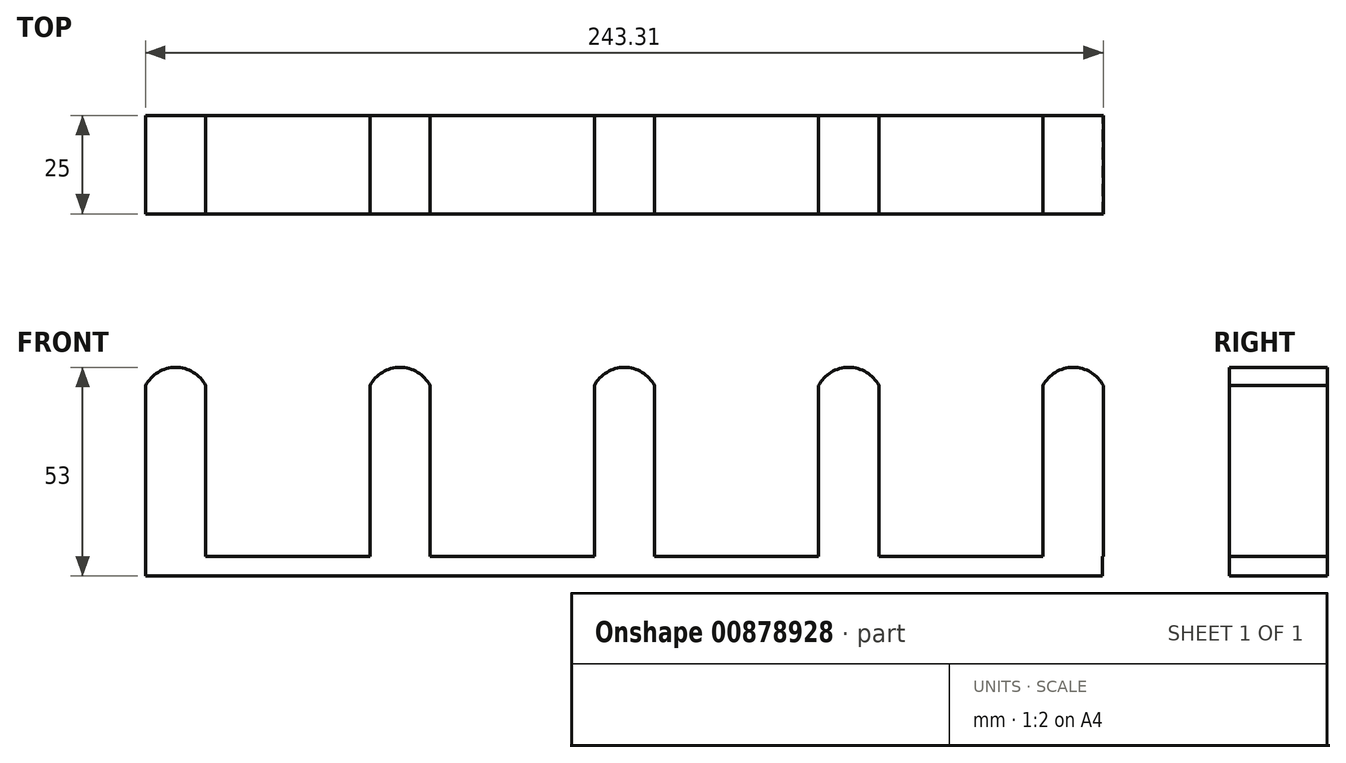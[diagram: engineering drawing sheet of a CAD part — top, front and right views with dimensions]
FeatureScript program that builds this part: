
annotation { "Feature Type Name" : "Feature", "Feature Type Description" : "" }
export const myFeature = defineFeature(function(context is Context, id is Id, definition is map)
    precondition{}
    {
        {
            var Q0;
            Q0=qCreatedBy(makeId("Front.planeOp"),FACE);
            var sketch = newSketch(context, id + "F0", { "sketchPlane" : qUnion([Q0])});
            skLineSegment(sketch, "E0", {"start": v(-65.05, 0) * mm, "end": v(83.37, 0) * mm});
            skLineSegment(sketch, "E1", {"start": v(-49.51, 48) * mm, "end": v(-49.51, -43.14) * mm, "construction": true});
            skLineSegment(sketch, "E2", {"start": v(-57.17, 0) * mm, "end": v(-57.17, 43.37) * mm});
            skLineSegment(sketch, "E3.MirrorCS", {"start": v(-41.86, 0) * mm, "end": v(-41.86, 43.37) * mm});
            skArc(sketch, "E4", {"start": v(-41.86, 43.37) * mm, "mid": v(-49.51, 48) * mm, "end": v(-57.17, 43.37) * mm});
            skLineSegment(sketch, "E5.1.0.0", {"start": v(-8.05, 0) * mm, "end": v(140.37, 0) * mm});
            skLineSegment(sketch, "E5.1.0.1", {"start": v(15.14, 0) * mm, "end": v(15.14, 43.37) * mm});
            skArc(sketch, "E5.1.0.2", {"start": v(15.14, 43.37) * mm, "mid": v(7.49, 48) * mm, "end": v(-0.17, 43.37) * mm});
            skLineSegment(sketch, "E5.1.0.3", {"start": v(-0.17, 0) * mm, "end": v(-0.17, 43.37) * mm});
            skLineSegment(sketch, "E5.1.0.4", {"start": v(7.49, 48) * mm, "end": v(7.49, -43.14) * mm, "construction": true});
            skLineSegment(sketch, "E5.2.0.0", {"start": v(48.95, 0) * mm, "end": v(197.37, 0) * mm});
            skLineSegment(sketch, "E5.2.0.1", {"start": v(72.14, 0) * mm, "end": v(72.14, 43.37) * mm});
            skArc(sketch, "E5.2.0.2", {"start": v(72.14, 43.37) * mm, "mid": v(64.49, 48) * mm, "end": v(56.83, 43.37) * mm});
            skLineSegment(sketch, "E5.2.0.3", {"start": v(56.83, 0) * mm, "end": v(56.83, 43.37) * mm});
            skLineSegment(sketch, "E5.2.0.4", {"start": v(64.49, 48) * mm, "end": v(64.49, -43.14) * mm, "construction": true});
            skLineSegment(sketch, "E5.direction1", {"start": v(-65.05, 0) * mm, "end": v(-8.05, 0) * mm, "construction": true});
            skLineSegment(sketch, "E6.bottom", {"start": v(-57.17, 0) * mm, "end": v(72.14, 0) * mm});
            skLineSegment(sketch, "E7.0.3.0", {"start": v(105.95, 0) * mm, "end": v(254.37, 0) * mm});
            skLineSegment(sketch, "E7.3.3.0", {"start": v(129.14, 0) * mm, "end": v(129.14, 43.37) * mm});
            skArc(sketch, "E7.6.3.0", {"start": v(129.14, 43.37) * mm, "mid": v(121.49, 48) * mm, "end": v(113.83, 43.37) * mm});
            skLineSegment(sketch, "E7.10.3.0", {"start": v(113.83, 0) * mm, "end": v(113.83, 43.37) * mm});
            skLineSegment(sketch, "E7.13.3.0", {"start": v(121.49, 48) * mm, "end": v(121.49, -43.14) * mm, "construction": true});
            skLineSegment(sketch, "E7.0.4.0", {"start": v(162.95, 0) * mm, "end": v(311.37, 0) * mm});
            skLineSegment(sketch, "E7.3.4.0", {"start": v(186.14, 0) * mm, "end": v(186.14, 43.37) * mm});
            skArc(sketch, "E7.6.4.0", {"start": v(186.14, 43.37) * mm, "mid": v(178.49, 48) * mm, "end": v(170.83, 43.37) * mm});
            skLineSegment(sketch, "E7.10.4.0", {"start": v(170.83, 0) * mm, "end": v(170.83, 43.37) * mm});
            skLineSegment(sketch, "E7.13.4.0", {"start": v(178.49, 48) * mm, "end": v(178.49, -43.14) * mm, "construction": true});
            skLineSegment(sketch, "E8.bottom", {"start": v(-57.17, 0) * mm, "end": v(185.89, 0) * mm});
            skLineSegment(sketch, "E8.top", {"start": v(-57.17, -4.99) * mm, "end": v(185.89, -4.99) * mm});
            skLineSegment(sketch, "E8.left", {"start": v(-57.17, 0) * mm, "end": v(-57.17, -4.99) * mm});
            skLineSegment(sketch, "E8.right", {"start": v(185.89, 0) * mm, "end": v(185.89, -4.99) * mm});
            skSolve(sketch);
        }
        {
            var Q0;
            {var subQ0=sQuery(id+"F0.wireOp",EDGE,"E2");Q0=makeQuery(id+"F0.imprint","IMPRINT",FACE,{"disambiguationData":[TD([[makeQuery(id+"F0.imprint","IMPRINT",EDGE,{"derivedFrom":subQ0}),-1.0]])]});}
            var Q1;
            {var subQ0=sQuery(id+"F0.wireOp",EDGE,"E5.1.0.1");Q1=makeQuery(id+"F0.imprint","IMPRINT",FACE,{"disambiguationData":[TD([[makeQuery(id+"F0.imprint","IMPRINT",EDGE,{"derivedFrom":subQ0}),1.0]])]});}
            var Q2;
            {var subQ0=sQuery(id+"F0.wireOp",EDGE,"E5.2.0.1");Q2=makeQuery(id+"F0.imprint","IMPRINT",FACE,{"disambiguationData":[TD([[makeQuery(id+"F0.imprint","IMPRINT",EDGE,{"derivedFrom":subQ0}),1.0]])]});}
            var Q3;
            Q3=makeQuery(id+"F0.imprint","IMPRINT",FACE,{"disambiguationData":[TD([[makeQuery(id+"F0.imprint","IMPRINT",EDGE,{"derivedFrom":sQuery(id+"F0.wireOp",EDGE,"E6.top")}),1.0]])]});
            var Q4;
            {var subQ0=sQuery(id+"F0.wireOp",EDGE,"E7.3.3.0");Q4=makeQuery(id+"F0.imprint","IMPRINT",FACE,{"disambiguationData":[TD([[makeQuery(id+"F0.imprint","IMPRINT",EDGE,{"derivedFrom":subQ0}),1.0]])]});}
            var Q5;
            {var subQ0=sQuery(id+"F0.wireOp",EDGE,"E7.3.4.0");Q5=makeQuery(id+"F0.imprint","IMPRINT",FACE,{"disambiguationData":[TD([[makeQuery(id+"F0.imprint","IMPRINT",EDGE,{"derivedFrom":subQ0}),1.0]])]});}
            var Q6;
            {var subQ0=sQuery(id+"F0.wireOp",EDGE,"E7.3.5.0");Q6=makeQuery(id+"F0.imprint","IMPRINT",FACE,{"disambiguationData":[TD([[makeQuery(id+"F0.imprint","IMPRINT",EDGE,{"derivedFrom":subQ0}),1.0]])]});}
            var Q7;
            Q7=makeQuery(id+"F0.imprint","IMPRINT",FACE,{"disambiguationData":[TD([[makeQuery(id+"F0.imprint","IMPRINT",EDGE,{"derivedFrom":sQuery(id+"F0.wireOp",EDGE,"E8.top")}),1.0]])]});
            extrude(context, id + "F1", {"entities" : qUnion([Q0, Q1, Q2, Q3, Q4, Q5, Q6, Q7]), "depth" : 25 * mm, "offsetDistance" : 25 * mm});
        }
    });
